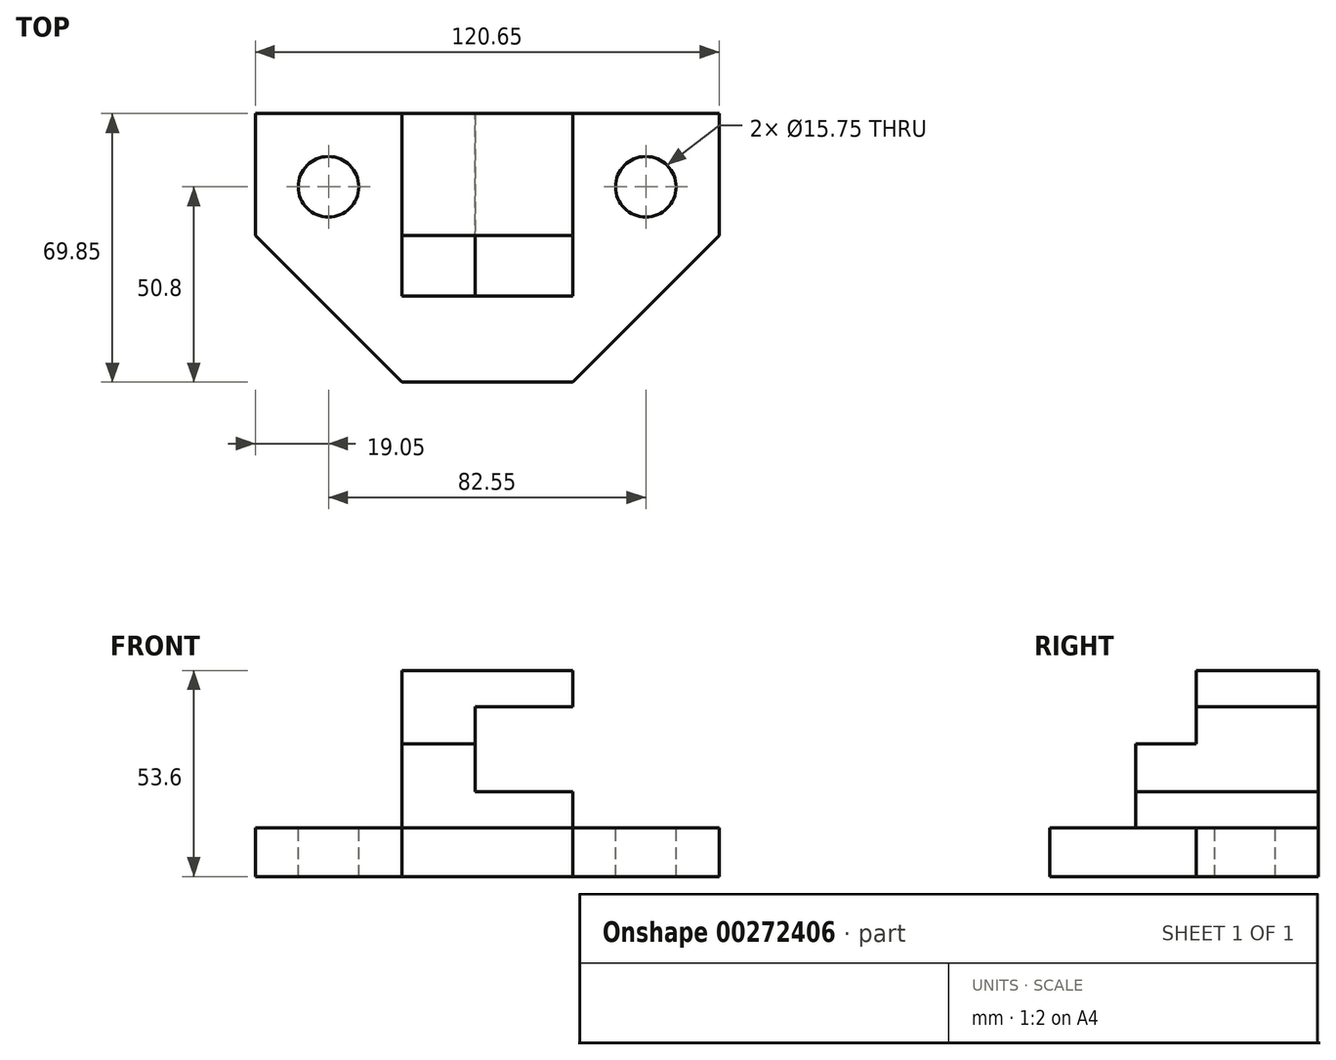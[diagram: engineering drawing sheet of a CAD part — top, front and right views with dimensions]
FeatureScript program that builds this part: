
annotation { "Feature Type Name" : "Feature", "Feature Type Description" : "" }
export const myFeature = defineFeature(function(context is Context, id is Id, definition is map)
    precondition{}
    {
        {
            var Q0;
            Q0=qCreatedBy(makeId("Front.planeOp"),FACE);
            var sketch = newSketch(context, id + "F0", { "sketchPlane" : qUnion([Q0])});
            skLineSegment(sketch, "E0", {"start": v(-59.4, -17.52) * mm, "end": v(61.24, -17.52) * mm});
            skLineSegment(sketch, "E1", {"start": v(-59.4, -17.52) * mm, "end": v(-59.4, -4.82) * mm});
            skLineSegment(sketch, "E2", {"start": v(-59.4, -4.82) * mm, "end": v(61.24, -4.82) * mm});
            skLineSegment(sketch, "E3", {"start": v(61.24, -4.82) * mm, "end": v(61.24, -17.52) * mm});
            skSolve(sketch);
        }
        {
            var Q0;
            Q0 = qSketchRegion(id + "F0", true);
            extrude(context, id + "F1", {"entities" : qUnion([Q0]), "depth" : 69.85 * mm});
        }
        {
            var Q0;
            Q0=makeQuery(id+"F1.opExtrude","SWEPT_FACE",FACE,{"disambiguationData":[OSD([sQuery(id+"F0.wireOp",EDGE,"E2")])]});
            var sketch = newSketch(context, id + "F2", { "sketchPlane" : qUnion([Q0])});
            skLineSegment(sketch, "E4", {"start": v(61.24, 0) * mm, "end": v(42.2, 0) * mm});
            skLineSegment(sketch, "E5", {"start": v(61.24, 0) * mm, "end": v(61.24, -19.05) * mm});
            skCircle(sketch, "E6", {"center": v(42.2, -19.05) * mm, "radius": 7.87 * mm});
            skLineSegment(sketch, "E7", {"start": v(-59.4, 0) * mm, "end": v(-40.36, 0) * mm});
            skLineSegment(sketch, "E8", {"start": v(-59.4, 0) * mm, "end": v(-59.4, -19.05) * mm});
            skCircle(sketch, "E9", {"center": v(-40.36, -19.05) * mm, "radius": 7.87 * mm});
            skLineSegment(sketch, "E10", {"start": v(61.24, 0) * mm, "end": v(61.24, -31.75) * mm});
            skLineSegment(sketch, "E11", {"start": v(-59.4, -31.75) * mm, "end": v(-59.4, 0) * mm});
            skLineSegment(sketch, "E12", {"start": v(61.24, -69.85) * mm, "end": v(23.14, -69.85) * mm});
            skLineSegment(sketch, "E13", {"start": v(-59.4, -69.85) * mm, "end": v(-21.3, -69.85) * mm});
            skLineSegment(sketch, "E14", {"start": v(-59.4, -31.75) * mm, "end": v(-21.3, -69.85) * mm});
            skLineSegment(sketch, "E15", {"start": v(23.14, -69.85) * mm, "end": v(61.24, -31.75) * mm});
            skSolve(sketch);
        }
        {
            var Q0;
            Q0 = qSketchRegion(id + "F2", true);
            extrude(context, id + "F3", {"entities" : qUnion([Q0]), "operationType" : NewBodyOperationType.REMOVE, "oppositeDirection" : true, "depth" : 15.75 * mm});
        }
        {
            var Q0;
            Q0=makeQuery(id+"F1.opExtrude","SWEPT_FACE",FACE,{"disambiguationData":[OSD([sQuery(id+"F0.wireOp",EDGE,"E2")])]});
            var sketch = newSketch(context, id + "F4", { "sketchPlane" : qUnion([Q0])});
            skLineSegment(sketch, "E16", {"start": v(-59.4, 0) * mm, "end": v(-21.3, 0) * mm});
            skLineSegment(sketch, "E17", {"start": v(61.24, 0) * mm, "end": v(23.14, 0) * mm});
            skLineSegment(sketch, "E18", {"start": v(-21.3, 0) * mm, "end": v(23.14, 0) * mm});
            skLineSegment(sketch, "E19", {"start": v(23.14, 0) * mm, "end": v(23.14, -47.5) * mm});
            skLineSegment(sketch, "E20", {"start": v(-21.3, -47.5) * mm, "end": v(-21.3, 0) * mm});
            skLineSegment(sketch, "E21", {"start": v(-21.3, -47.5) * mm, "end": v(23.14, -47.5) * mm});
            skSolve(sketch);
        }
        {
            var Q0;
            {var subQ0=sQuery(id+"F2.wireOp",EDGE,"E13");Q0=makeQuery(id+"F2.imprint","IMPRINT",FACE,{"disambiguationData":[TD([[makeQuery(id+"F2.imprint","IMPRINT",EDGE,{"derivedFrom":subQ0}),1.0]])]});}
            var Q1;
            {var subQ0=sQuery(id+"F2.wireOp",EDGE,"E12");Q1=makeQuery(id+"F2.imprint","IMPRINT",FACE,{"disambiguationData":[TD([[makeQuery(id+"F2.imprint","IMPRINT",EDGE,{"derivedFrom":subQ0}),1.0]])]});}
            extrude(context, id + "F5", {"entities" : qUnion([Q0, Q1]), "operationType" : NewBodyOperationType.REMOVE, "oppositeDirection" : true, "depth" : 12.7 * mm});
        }
        {
            var Q0;
            Q0=makeQuery(id+"F4.imprint","IMPRINT",FACE,{"disambiguationData":[TD([[makeQuery(id+"F4.imprint","IMPRINT",EDGE,{"derivedFrom":sQuery(id+"F4.wireOp",EDGE,"E18")}),-1.0]])]});
            extrude(context, id + "F6", {"entities" : qUnion([Q0]), "operationType" : NewBodyOperationType.ADD, "depth" : 40.9 * mm});
        }
        {
            var Q0;
            Q0=makeQuery(id+"F6.opExtrude","SWEPT_FACE",FACE,{"disambiguationData":[OSD([sQuery(id+"F4.wireOp",EDGE,"E19")])]});
            var sketch = newSketch(context, id + "F7", { "sketchPlane" : qUnion([Q0])});
            skLineSegment(sketch, "E22", {"start": v(0, 36.08) * mm, "end": v(0, 26.68) * mm});
            skLineSegment(sketch, "E23", {"start": v(0, 26.68) * mm, "end": v(-47.5, 26.68) * mm});
            skLineSegment(sketch, "E24", {"start": v(-47.5, 26.68) * mm, "end": v(-47.5, 36.08) * mm});
            skLineSegment(sketch, "E25", {"start": v(-47.5, 36.08) * mm, "end": v(0, 36.08) * mm});
            skLineSegment(sketch, "E26", {"start": v(-47.5, -4.82) * mm, "end": v(-47.5, 4.58) * mm});
            skLineSegment(sketch, "E27", {"start": v(-47.5, 4.58) * mm, "end": v(0, 4.58) * mm});
            skLineSegment(sketch, "E28", {"start": v(0, 4.58) * mm, "end": v(0, -4.82) * mm});
            skLineSegment(sketch, "E29", {"start": v(0, -4.82) * mm, "end": v(-47.5, -4.82) * mm});
            skLineSegment(sketch, "E30", {"start": v(-47.5, 26.68) * mm, "end": v(-47.5, 4.58) * mm});
            skLineSegment(sketch, "E31", {"start": v(0, 26.68) * mm, "end": v(0, 4.58) * mm});
            skSolve(sketch);
        }
        {
            var Q0;
            Q0=makeQuery(id+"F7.imprint","IMPRINT",FACE,{"disambiguationData":[TD([[makeQuery(id+"F7.imprint","IMPRINT",EDGE,{"derivedFrom":sQuery(id+"F7.wireOp",EDGE,"E23")}),1.0]])]});
            extrude(context, id + "F8", {"entities" : qUnion([Q0]), "operationType" : NewBodyOperationType.REMOVE, "oppositeDirection" : true, "depth" : 25.4 * mm});
        }
        {
            var Q0;
            Q0=makeQuery(id+"F6.opExtrude","SWEPT_FACE",FACE,{"disambiguationData":[OSD([sQuery(id+"F4.wireOp",EDGE,"E20")])]});
            var sketch = newSketch(context, id + "F9", { "sketchPlane" : qUnion([Q0])});
            skLineSegment(sketch, "E32", {"start": v(47.5, 36.08) * mm, "end": v(47.5, 17.03) * mm});
            skLineSegment(sketch, "E33", {"start": v(47.5, 17.03) * mm, "end": v(31.75, 17.03) * mm});
            skLineSegment(sketch, "E34", {"start": v(31.75, 17.03) * mm, "end": v(31.75, 36.08) * mm});
            skLineSegment(sketch, "E35", {"start": v(31.75, 36.08) * mm, "end": v(47.5, 36.08) * mm});
            skSolve(sketch);
        }
        {
            var Q0;
            Q0=makeQuery(id+"F9.imprint","IMPRINT",FACE,{"disambiguationData":[TD([[makeQuery(id+"F9.imprint","IMPRINT",EDGE,{"derivedFrom":sQuery(id+"F9.wireOp",EDGE,"E32")}),-1.0]])]});
            extrude(context, id + "F10", {"entities" : qUnion([Q0]), "operationType" : NewBodyOperationType.REMOVE, "oppositeDirection" : true, "depth" : 44.45 * mm});
        }
    });
